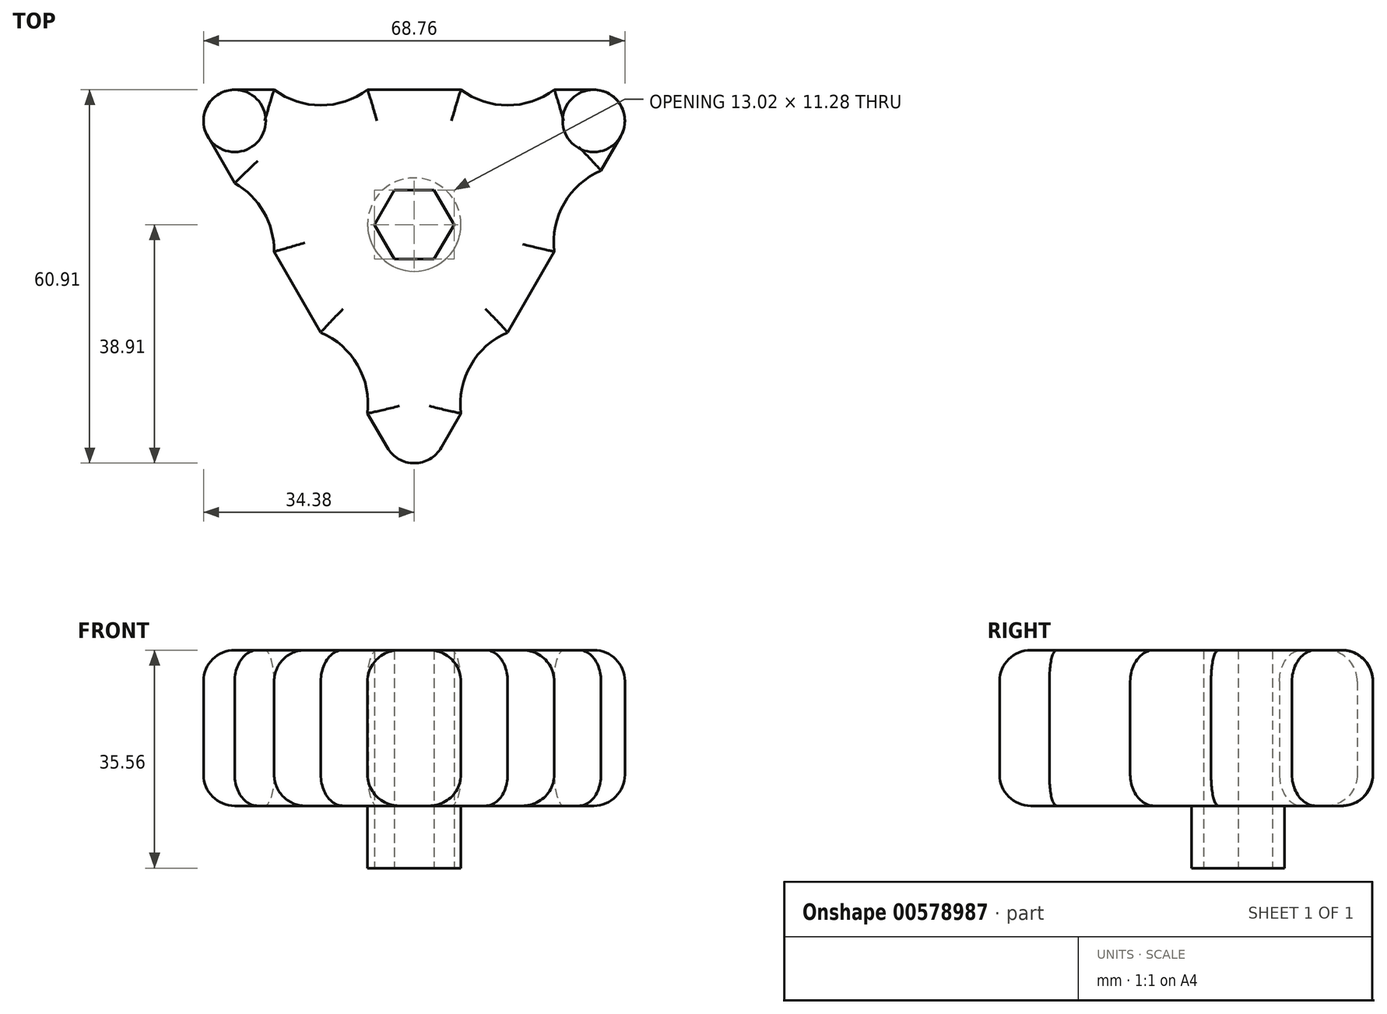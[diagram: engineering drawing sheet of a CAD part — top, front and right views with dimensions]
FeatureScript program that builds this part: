
annotation { "Feature Type Name" : "Feature", "Feature Type Description" : "" }
export const myFeature = defineFeature(function(context is Context, id is Id, definition is map)
    precondition{}
    {
        {
            var Q0;
            Q0=qCreatedBy(makeId("Top.planeOp"),FACE);
            var sketch = newSketch(context, id + "F0", { "sketchPlane" : qUnion([Q0])});
            skCircle(sketch, "E0.cCircle", {"center": v(0, 0) * mm, "radius": 22 * mm, "construction": true});
            skLineSegment(sketch, "E0.0", {"start": v(-38.1, 22) * mm, "end": v(-22.86, 22) * mm});
            skLineSegment(sketch, "E0.1", {"start": v(38.1, 22) * mm, "end": v(30.48, 8.8) * mm});
            skLineSegment(sketch, "E0.2", {"start": v(0, -44) * mm, "end": v(-7.62, -30.8) * mm});
            skPoint(sketch, "E0.0.midPoint", {"position": v(0, 22) * mm});
            skLineSegment(sketch, "E1", {"start": v(-7.62, 22) * mm, "end": v(7.62, 22) * mm});
            skLineSegment(sketch, "E2", {"start": v(22.86, 22) * mm, "end": v(38.1, 22) * mm});
            skArc(sketch, "E3", {"start": v(-22.86, 22) * mm, "mid": v(-15.24, 19.46) * mm, "end": v(-7.62, 22) * mm});
            skArc(sketch, "E4", {"start": v(7.62, 22) * mm, "mid": v(15.24, 19.46) * mm, "end": v(22.86, 22) * mm});
            skLineSegment(sketch, "E5", {"start": v(-29.3, 6.76) * mm, "end": v(-38.1, 22) * mm});
            skLineSegment(sketch, "E6", {"start": v(-15.24, -17.6) * mm, "end": v(-22.86, -4.4) * mm});
            skLineSegment(sketch, "E7", {"start": v(7.62, -30.8) * mm, "end": v(0, -44) * mm});
            skLineSegment(sketch, "E8", {"start": v(22.86, -4.4) * mm, "end": v(15.24, -17.6) * mm});
            skArc(sketch, "E9", {"start": v(30.48, 8.8) * mm, "mid": v(24.47, 3.47) * mm, "end": v(22.86, -4.4) * mm});
            skArc(sketch, "E10", {"start": v(15.24, -17.6) * mm, "mid": v(9.23, -22.93) * mm, "end": v(7.62, -30.8) * mm});
            skArc(sketch, "E11", {"start": v(-7.62, -30.8) * mm, "mid": v(-9.23, -22.93) * mm, "end": v(-15.24, -17.6) * mm});
            skArc(sketch, "E12", {"start": v(-22.86, -4.4) * mm, "mid": v(-24.56, 2.06) * mm, "end": v(-29.3, 6.76) * mm});
            skSolve(sketch);
        }
        {
            var Q0;
            Q0 = qSketchRegion(id + "F0", true);
            extrude(context, id + "F1", {"entities" : qUnion([Q0]), "depth" : 25.4 * mm, "offsetDistance" : 25.4 * mm});
        }
        {
            var Q0;
            Q0=makeQuery(id+"F1.opExtrude","CAP_FACE",FACE,{"disambiguationData":[OSD([sQuery(id+"F0.wireOp",EDGE,"E0.0"),sQuery(id+"F0.wireOp",EDGE,"E0.1"),sQuery(id+"F0.wireOp",EDGE,"E0.2"),sQuery(id+"F0.wireOp",EDGE,"E1"),sQuery(id+"F0.wireOp",EDGE,"E2"),sQuery(id+"F0.wireOp",EDGE,"E3"),sQuery(id+"F0.wireOp",EDGE,"E4"),sQuery(id+"F0.wireOp",EDGE,"E5"),sQuery(id+"F0.wireOp",EDGE,"E6"),sQuery(id+"F0.wireOp",EDGE,"E7"),sQuery(id+"F0.wireOp",EDGE,"E8"),sQuery(id+"F0.wireOp",EDGE,"E9"),sQuery(id+"F0.wireOp",EDGE,"E10"),sQuery(id+"F0.wireOp",EDGE,"E11"),sQuery(id+"F0.wireOp",EDGE,"E12")])],"isStart":false});
            fillet(context, id + "F2", {"entities" : qUnion([Q0]), "radius" : 5.08 * mm, "tangentPropagation" : true, "allowEdgeOverflow" : false});
        }
        {
            var Q0;
            Q0=makeQuery(id+"F1.opExtrude","CAP_FACE",FACE,{"disambiguationData":[OSD([sQuery(id+"F0.wireOp",EDGE,"E0.0"),sQuery(id+"F0.wireOp",EDGE,"E0.1"),sQuery(id+"F0.wireOp",EDGE,"E0.2"),sQuery(id+"F0.wireOp",EDGE,"E1"),sQuery(id+"F0.wireOp",EDGE,"E2"),sQuery(id+"F0.wireOp",EDGE,"E3"),sQuery(id+"F0.wireOp",EDGE,"E4"),sQuery(id+"F0.wireOp",EDGE,"E5"),sQuery(id+"F0.wireOp",EDGE,"E6"),sQuery(id+"F0.wireOp",EDGE,"E7"),sQuery(id+"F0.wireOp",EDGE,"E8"),sQuery(id+"F0.wireOp",EDGE,"E9"),sQuery(id+"F0.wireOp",EDGE,"E10"),sQuery(id+"F0.wireOp",EDGE,"E11"),sQuery(id+"F0.wireOp",EDGE,"E12")])],"isStart":true});
            fillet(context, id + "F3", {"entities" : qUnion([Q0]), "radius" : 5.08 * mm, "tangentPropagation" : true, "allowEdgeOverflow" : false});
        }
        {
            var Q0;
            Q0=makeQuery(id+"F2.opFillet","BLEND_EDGE",EDGE,{"blendedFrom":[makeQuery(id+"F1.opExtrude","CAP_EDGE",EDGE,{"disambiguationData":[OSD([sQuery(id+"F0.wireOp",EDGE,"E0.0")])],"isStart":false}),makeQuery(id+"F1.opExtrude","CAP_EDGE",EDGE,{"disambiguationData":[OSD([sQuery(id+"F0.wireOp",EDGE,"E5")])],"isStart":false})],"blendedInto":[]});
            var Q1;
            Q1=makeQuery(id+"F2.opFillet","BLEND_EDGE",EDGE,{"blendedFrom":[makeQuery(id+"F1.opExtrude","CAP_EDGE",EDGE,{"disambiguationData":[OSD([sQuery(id+"F0.wireOp",EDGE,"E0.1")])],"isStart":false}),makeQuery(id+"F1.opExtrude","CAP_EDGE",EDGE,{"disambiguationData":[OSD([sQuery(id+"F0.wireOp",EDGE,"E2")])],"isStart":false})],"blendedInto":[]});
            var Q2;
            Q2=makeQuery(id+"F3.opFillet","BLEND_EDGE",EDGE,{"blendedFrom":[makeQuery(id+"F1.opExtrude","CAP_EDGE",EDGE,{"disambiguationData":[OSD([sQuery(id+"F0.wireOp",EDGE,"E0.2")])],"isStart":true}),makeQuery(id+"F1.opExtrude","CAP_EDGE",EDGE,{"disambiguationData":[OSD([sQuery(id+"F0.wireOp",EDGE,"E7")])],"isStart":true})],"blendedInto":[]});
            fillet(context, id + "F4", {"entities" : qUnion([Q0, Q1, Q2]), "radius" : 5.08 * mm, "tangentPropagation" : true, "allowEdgeOverflow" : false});
        }
        {
            var Q0;
            Q0=makeQuery(id+"F1.opExtrude","CAP_FACE",FACE,{"disambiguationData":[OSD([sQuery(id+"F0.wireOp",EDGE,"E0.0"),sQuery(id+"F0.wireOp",EDGE,"E0.1"),sQuery(id+"F0.wireOp",EDGE,"E0.2"),sQuery(id+"F0.wireOp",EDGE,"E1"),sQuery(id+"F0.wireOp",EDGE,"E2"),sQuery(id+"F0.wireOp",EDGE,"E3"),sQuery(id+"F0.wireOp",EDGE,"E4"),sQuery(id+"F0.wireOp",EDGE,"E5"),sQuery(id+"F0.wireOp",EDGE,"E6"),sQuery(id+"F0.wireOp",EDGE,"E7"),sQuery(id+"F0.wireOp",EDGE,"E8"),sQuery(id+"F0.wireOp",EDGE,"E9"),sQuery(id+"F0.wireOp",EDGE,"E10"),sQuery(id+"F0.wireOp",EDGE,"E11"),sQuery(id+"F0.wireOp",EDGE,"E12")])],"isStart":true});
            var sketch = newSketch(context, id + "F5", { "sketchPlane" : qUnion([Q0])});
            skCircle(sketch, "E13", {"center": v(0, 0) * mm, "radius": 7.62 * mm});
            skSolve(sketch);
        }
        {
            var Q0;
            Q0 = qSketchRegion(id + "F5", true);
            extrude(context, id + "F6", {"entities" : qUnion([Q0]), "operationType" : NewBodyOperationType.ADD, "depth" : 10.16 * mm, "offsetDistance" : 25.4 * mm});
        }
        {
            var Q0;
            Q0=makeQuery(id+"F6.opExtrude","CAP_FACE",FACE,{"disambiguationData":[OSD([sQuery(id+"F5.wireOp",EDGE,"E13")])],"isStart":false});
            var sketch = newSketch(context, id + "F7", { "sketchPlane" : qUnion([Q0])});
            skCircle(sketch, "E14.cCircle", {"center": v(0, 0) * mm, "radius": 5.64 * mm, "construction": true});
            skLineSegment(sketch, "E14.0", {"start": v(3.26, -5.64) * mm, "end": v(-3.26, -5.64) * mm});
            skLineSegment(sketch, "E14.1", {"start": v(-3.26, -5.64) * mm, "end": v(-6.51, 0) * mm});
            skLineSegment(sketch, "E14.2", {"start": v(-6.51, 0) * mm, "end": v(-3.26, 5.64) * mm});
            skLineSegment(sketch, "E14.3", {"start": v(-3.26, 5.64) * mm, "end": v(3.26, 5.64) * mm});
            skLineSegment(sketch, "E14.4", {"start": v(3.26, 5.64) * mm, "end": v(6.51, 0) * mm});
            skLineSegment(sketch, "E14.5", {"start": v(6.51, 0) * mm, "end": v(3.26, -5.64) * mm});
            skPoint(sketch, "E14.0.midPoint", {"position": v(0, -5.64) * mm});
            skSolve(sketch);
        }
        {
            var Q0;
            Q0 = qSketchRegion(id + "F7", true);
            extrude(context, id + "F8", {"entities" : qUnion([Q0]), "operationType" : NewBodyOperationType.REMOVE, "oppositeDirection" : true, "depth" : 38.1 * mm, "offsetDistance" : 25.4 * mm});
        }
    });
